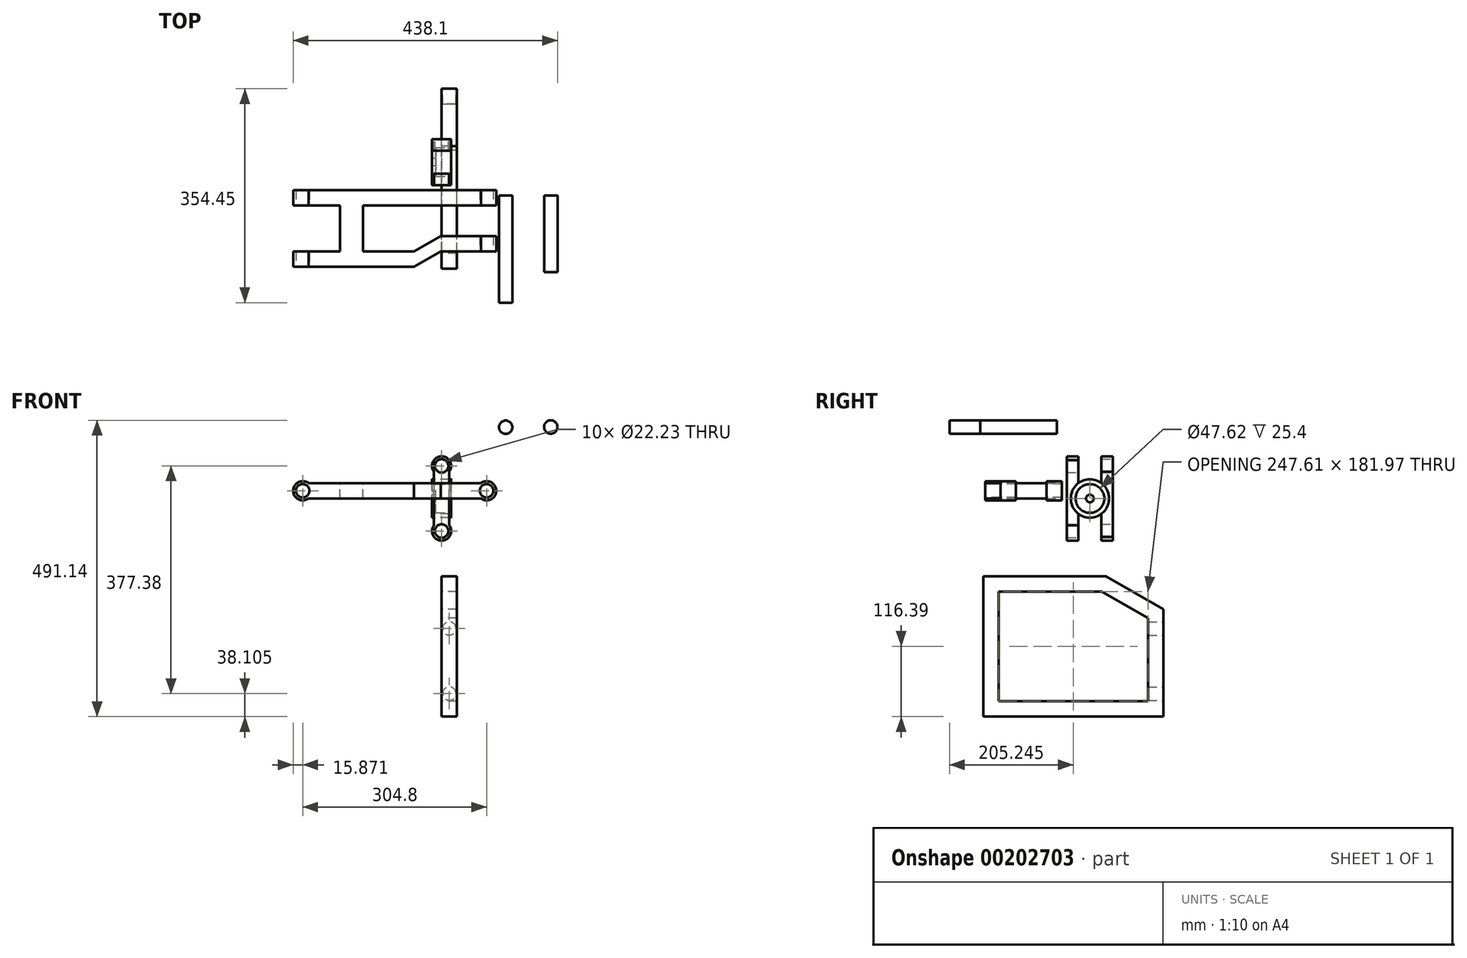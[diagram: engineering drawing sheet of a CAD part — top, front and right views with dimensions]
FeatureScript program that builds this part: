
annotation { "Feature Type Name" : "Feature", "Feature Type Description" : "" }
export const myFeature = defineFeature(function(context is Context, id is Id, definition is map)
    precondition{}
    {
        {
            var Q0;
            Q0=qCreatedBy(makeId("Top.planeOp"),FACE);
            var sketch = newSketch(context, id + "F0", { "sketchPlane" : qUnion([Q0])});
            skLineSegment(sketch, "E0.bottom", {"start": v(-230.2, 8.47) * mm, "end": v(74.6, 8.47) * mm});
            skLineSegment(sketch, "E0.top", {"start": v(-230.2, -16.93) * mm, "end": v(74.6, -16.93) * mm});
            skLineSegment(sketch, "E0.left", {"start": v(-230.2, 8.47) * mm, "end": v(-230.2, -16.93) * mm});
            skLineSegment(sketch, "E0.right", {"start": v(74.6, 8.47) * mm, "end": v(74.6, -16.93) * mm});
            skLineSegment(sketch, "E1", {"start": v(-77.8, -16.93) * mm, "end": v(-77.8, -93.13) * mm, "construction": true});
            skLineSegment(sketch, "E2", {"start": v(-230.2, -55.03) * mm, "end": v(91.79, -55.03) * mm, "construction": true});
            skPoint(sketch, "E2.startSnap0", {"position": v(-77.8, -55.03) * mm});
            skLineSegment(sketch, "E3.MirrorCS", {"start": v(-230.2, -118.53) * mm, "end": v(-45.6, -118.53) * mm});
            skLineSegment(sketch, "E4.MirrorCS", {"start": v(-230.2, -93.13) * mm, "end": v(-45.6, -93.13) * mm});
            skLineSegment(sketch, "E5.MirrorCS", {"start": v(-230.2, -118.53) * mm, "end": v(-230.2, -93.13) * mm});
            skLineSegment(sketch, "E6.bottom", {"start": v(74.6, -93.13) * mm, "end": v(74.6, -93.13) * mm});
            skLineSegment(sketch, "E6.top", {"start": v(74.6, -67.73) * mm, "end": v(74.6, -67.73) * mm});
            skLineSegment(sketch, "E6.left", {"start": v(74.6, -93.13) * mm, "end": v(74.6, -67.73) * mm});
            skLineSegment(sketch, "E6.right", {"start": v(74.6, -93.13) * mm, "end": v(74.6, -67.73) * mm});
            skLineSegment(sketch, "E7.bottom", {"start": v(74.6, -67.73) * mm, "end": v(-1.6, -67.73) * mm});
            skLineSegment(sketch, "E7.top", {"start": v(74.6, -67.73) * mm, "end": v(-1.6, -67.73) * mm});
            skLineSegment(sketch, "E7.right", {"start": v(-1.6, -67.73) * mm, "end": v(-1.6, -67.73) * mm});
            skLineSegment(sketch, "E8", {"start": v(-1.6, -67.73) * mm, "end": v(-45.6, -93.13) * mm});
            skLineSegment(sketch, "E9", {"start": v(-45.6, -118.53) * mm, "end": v(-1.6, -93.13) * mm});
            skLineSegment(sketch, "E10.trimOffspring", {"start": v(-1.6, -93.13) * mm, "end": v(74.6, -93.13) * mm});
            skSolve(sketch);
        }
        {
            var Q0;
            Q0 = qSketchRegion(id + "F0", true);
            extrude(context, id + "F1", {"entities" : qUnion([Q0]), "depth" : 25.4 * mm});
        }
        {
            var Q0;
            Q0=makeQuery(id+"F1.opExtrude","SWEPT_FACE",FACE,{"disambiguationData":[OSD([sQuery(id+"F0.wireOp",EDGE,"E3.MirrorCS")])]});
            var sketch = newSketch(context, id + "F2", { "sketchPlane" : qUnion([Q0])});
            skCircle(sketch, "E11", {"center": v(-230.2, 12.7) * mm, "radius": 15.88 * mm});
            skSolve(sketch);
        }
        {
            var Q0;
            Q0=makeQuery(id+"F1.opExtrude","SWEPT_FACE",FACE,{"disambiguationData":[OSD([sQuery(id+"F0.wireOp",EDGE,"E10.trimOffspring")])]});
            var sketch = newSketch(context, id + "F3", { "sketchPlane" : qUnion([Q0])});
            skCircle(sketch, "E12", {"center": v(74.6, 12.7) * mm, "radius": 15.88 * mm});
            skSolve(sketch);
        }
        {
            var Q0;
            {var subQ1=sQuery(id+"F0.wireOp",EDGE,"E3.MirrorCS");var subQ6=makeQuery(id+"F1.opExtrude","SWEPT_EDGE",EDGE,{"disambiguationData":[OSD([subQ1,sQuery(id+"F0.wireOp",EDGE,"E5.MirrorCS")])]});Q0=makeQuery(id+"F2.imprint","IMPRINT",FACE,{"disambiguationData":[TD([[makeQuery(id+"F2.imprint","IMPRINT",EDGE,{"derivedFrom":subQ6}),-1.0]])]});}
            extrude(context, id + "F4", {"entities" : qUnion([Q0]), "operationType" : NewBodyOperationType.ADD, "oppositeDirection" : true, "depth" : 25.4 * mm});
        }
        {
            var Q0;
            {var subQ1=sQuery(id+"F0.wireOp",EDGE,"E10.trimOffspring");var subQ6=makeQuery(id+"F1.opExtrude","SWEPT_EDGE",EDGE,{"disambiguationData":[OSD([sQuery(id+"F0.wireOp",EDGE,"E6.right"),subQ1])]});Q0=makeQuery(id+"F3.imprint","IMPRINT",FACE,{"disambiguationData":[TD([[makeQuery(id+"F3.imprint","IMPRINT",EDGE,{"derivedFrom":subQ6}),1.0]])]});}
            extrude(context, id + "F5", {"entities" : qUnion([Q0]), "operationType" : NewBodyOperationType.ADD, "oppositeDirection" : true, "depth" : 25.4 * mm});
        }
        {
            var Q0;
            Q0=makeQuery(id+"F1.opExtrude","SWEPT_FACE",FACE,{"disambiguationData":[OSD([sQuery(id+"F0.wireOp",EDGE,"E0.bottom")])]});
            var sketch = newSketch(context, id + "F6", { "sketchPlane" : qUnion([Q0])});
            skCircle(sketch, "E13", {"center": v(-74.6, 12.7) * mm, "radius": 15.88 * mm});
            skCircle(sketch, "E14", {"center": v(230.2, 12.7) * mm, "radius": 15.88 * mm});
            skSolve(sketch);
        }
        {
            var Q0;
            {var subQ1=sQuery(id+"F0.wireOp",EDGE,"E0.bottom");var subQ6=makeQuery(id+"F1.opExtrude","SWEPT_EDGE",EDGE,{"disambiguationData":[OSD([subQ1,sQuery(id+"F0.wireOp",EDGE,"E0.right")])]});Q0=makeQuery(id+"F6.imprint","IMPRINT",FACE,{"disambiguationData":[TD([[makeQuery(id+"F6.imprint","IMPRINT",EDGE,{"derivedFrom":subQ6}),-1.0]])]});}
            var Q1;
            {var subQ1=sQuery(id+"F0.wireOp",EDGE,"E0.bottom");var subQ6=makeQuery(id+"F1.opExtrude","SWEPT_EDGE",EDGE,{"disambiguationData":[OSD([subQ1,sQuery(id+"F0.wireOp",EDGE,"E0.left")])]});Q1=makeQuery(id+"F6.imprint","IMPRINT",FACE,{"disambiguationData":[TD([[makeQuery(id+"F6.imprint","IMPRINT",EDGE,{"derivedFrom":subQ6}),1.0]])]});}
            extrude(context, id + "F7", {"entities" : qUnion([Q0, Q1]), "operationType" : NewBodyOperationType.ADD, "oppositeDirection" : true, "depth" : 25.4 * mm});
        }
        {
            var Q0;
            {var subQ0=sQuery(id+"F0.wireOp",EDGE,"E3.MirrorCS");Q0=makeQuery(id+"F4.boolean.opBoolean","MERGE",FACE,{"derivedFrom":[makeQuery(id+"F1.opExtrude","SWEPT_FACE",FACE,{"disambiguationData":[OSD([subQ0])]}),makeQuery(id+"F4.opExtrude","CAP_FACE",FACE,{"disambiguationData":[OSD([subQ0,sQuery(id+"F0.wireOp",EDGE,"E5.MirrorCS"),sQuery(id+"F2.wireOp",EDGE,"E11")])],"isStart":true})]});}
            var sketch = newSketch(context, id + "F8", { "sketchPlane" : qUnion([Q0])});
            skCircle(sketch, "E15", {"center": v(-230.2, 12.7) * mm, "radius": 11.11 * mm});
            skSolve(sketch);
        }
        {
            var Q0;
            Q0=makeQuery(id+"F8.imprint","IMPRINT",FACE,{"disambiguationData":[TD([[makeQuery(id+"F8.imprint","IMPRINT",EDGE,{"derivedFrom":sQuery(id+"F8.wireOp",EDGE,"E15")}),1.0]])]});
            extrude(context, id + "F9", {"entities" : qUnion([Q0]), "operationType" : NewBodyOperationType.REMOVE, "endBound" : BoundingType.THROUGH_ALL, "oppositeDirection" : true, "depth" : 25.4 * mm});
        }
        {
            var Q0;
            {var subQ0=sQuery(id+"F0.wireOp",EDGE,"E10.trimOffspring");Q0=makeQuery(id+"F5.boolean.opBoolean","MERGE",FACE,{"derivedFrom":[makeQuery(id+"F1.opExtrude","SWEPT_FACE",FACE,{"disambiguationData":[OSD([subQ0])]}),makeQuery(id+"F5.opExtrude","CAP_FACE",FACE,{"disambiguationData":[OSD([sQuery(id+"F0.wireOp",EDGE,"E6.right"),subQ0,sQuery(id+"F3.wireOp",EDGE,"E12")])],"isStart":true})]});}
            var sketch = newSketch(context, id + "F10", { "sketchPlane" : qUnion([Q0])});
            skCircle(sketch, "E16", {"center": v(74.6, 12.7) * mm, "radius": 11.11 * mm});
            skSolve(sketch);
        }
        {
            var Q0;
            Q0=makeQuery(id+"F10.imprint","IMPRINT",FACE,{"disambiguationData":[TD([[makeQuery(id+"F10.imprint","IMPRINT",EDGE,{"derivedFrom":sQuery(id+"F10.wireOp",EDGE,"E16")}),1.0]])]});
            extrude(context, id + "F11", {"entities" : qUnion([Q0]), "operationType" : NewBodyOperationType.REMOVE, "endBound" : BoundingType.THROUGH_ALL, "oppositeDirection" : true, "depth" : 25.4 * mm});
        }
        {
            var Q0;
            {var subQ0=sQuery(id+"F0.wireOp",EDGE,"E0.bottom");Q0=makeQuery(id+"F7.boolean.opBoolean","MERGE",FACE,{"derivedFrom":[makeQuery(id+"F1.opExtrude","SWEPT_FACE",FACE,{"disambiguationData":[OSD([subQ0])]}),makeQuery(id+"F7.opExtrude","CAP_FACE",FACE,{"disambiguationData":[OSD([subQ0,sQuery(id+"F0.wireOp",EDGE,"E0.right"),sQuery(id+"F6.wireOp",EDGE,"E13")])],"isStart":true}),makeQuery(id+"F7.opExtrude","CAP_FACE",FACE,{"disambiguationData":[OSD([subQ0,sQuery(id+"F0.wireOp",EDGE,"E0.left"),sQuery(id+"F6.wireOp",EDGE,"E14")])],"isStart":true})]});}
            var sketch = newSketch(context, id + "F12", { "sketchPlane" : qUnion([Q0])});
            skCircle(sketch, "E17", {"center": v(-74.6, 12.7) * mm, "radius": 11.11 * mm});
            skCircle(sketch, "E18", {"center": v(230.2, 12.7) * mm, "radius": 11.11 * mm});
            skSolve(sketch);
        }
        {
            var Q0;
            Q0=makeQuery(id+"F12.imprint","IMPRINT",FACE,{"disambiguationData":[TD([[makeQuery(id+"F12.imprint","IMPRINT",EDGE,{"derivedFrom":sQuery(id+"F12.wireOp",EDGE,"E17")}),1.0]])]});
            var Q1;
            Q1=makeQuery(id+"F12.imprint","IMPRINT",FACE,{"disambiguationData":[TD([[makeQuery(id+"F12.imprint","IMPRINT",EDGE,{"derivedFrom":sQuery(id+"F12.wireOp",EDGE,"E18")}),1.0]])]});
            extrude(context, id + "F13", {"entities" : qUnion([Q0, Q1]), "operationType" : NewBodyOperationType.REMOVE, "endBound" : BoundingType.THROUGH_ALL, "oppositeDirection" : true, "depth" : 25.4 * mm});
        }
        {
            var Q0;
            Q0=makeQuery(id+"F1.opExtrude","CAP_FACE",FACE,{"disambiguationData":[OSD([sQuery(id+"F0.wireOp",EDGE,"E0.bottom"),sQuery(id+"F0.wireOp",EDGE,"E0.top"),sQuery(id+"F0.wireOp",EDGE,"E0.left"),sQuery(id+"F0.wireOp",EDGE,"E0.right")])],"isStart":false});
            var sketch = newSketch(context, id + "F14", { "sketchPlane" : qUnion([Q0])});
            skLineSegment(sketch, "E19", {"start": v(-77.8, -16.93) * mm, "end": v(-220.68, -16.93) * mm});
            skLineSegment(sketch, "E20.bottom", {"start": v(-168.3, -10.98) * mm, "end": v(-130.2, -10.98) * mm});
            skLineSegment(sketch, "E20.top", {"start": v(-168.3, -103.03) * mm, "end": v(-130.2, -103.03) * mm});
            skLineSegment(sketch, "E20.left", {"start": v(-168.3, -10.98) * mm, "end": v(-168.3, -103.03) * mm});
            skLineSegment(sketch, "E20.right", {"start": v(-130.2, -10.98) * mm, "end": v(-130.2, -103.03) * mm});
            skLineSegment(sketch, "E21", {"start": v(-149.25, -16.93) * mm, "end": v(-149.25, -93.19) * mm, "construction": true});
            skSolve(sketch);
        }
        {
            var Q0;
            {var subQ5=sQuery(id+"F14.wireOp",EDGE,"E20.top");Q0=makeQuery(id+"F14.imprint","IMPRINT",FACE,{"disambiguationData":[TD([[makeQuery(id+"F14.imprint","IMPRINT",EDGE,{"derivedFrom":subQ5}),1.0]])]});}
            extrude(context, id + "F15", {"entities" : qUnion([Q0]), "operationType" : NewBodyOperationType.ADD, "oppositeDirection" : true, "depth" : 25.4 * mm});
        }
        {
            var Q0;
            Q0=makeQuery(id+"F15.opExtrude","SWEPT_FACE",FACE,{"disambiguationData":[OSD([sQuery(id+"F14.wireOp",EDGE,"E20.left")])]});
            extrude(context, id + "F16", {"entities" : qUnion([Q0]), "depth" : 25.4 * mm});
        }
        {
            var Q0;
            Q0=makeQuery(id+"F16.opExtrude","SWEPT_BODY",BODY,{"disambiguationData":[OSD([sQuery(id+"F14.wireOp",EDGE,"E20.left")])]});
            deleteBodies(context, id + "F17", {"entities" : qUnion([Q0])});
        }
        {
            var Q0;
            Q0=qCreatedBy(makeId("Right.planeOp"),FACE);
            var sketch = newSketch(context, id + "F18", { "sketchPlane" : qUnion([Q0])});
            skLineSegment(sketch, "E22", {"start": v(17, 63.5) * mm, "end": v(36.05, 63.5) * mm});
            skLineSegment(sketch, "E23", {"start": v(36.05, 63.5) * mm, "end": v(36.05, 12.7) * mm});
            skLineSegment(sketch, "E24", {"start": v(36.05, 12.7) * mm, "end": v(74.15, 12.7) * mm});
            skLineSegment(sketch, "E25", {"start": v(74.15, 12.7) * mm, "end": v(74.15, 63.5) * mm});
            skLineSegment(sketch, "E26", {"start": v(74.15, 63.5) * mm, "end": v(93.2, 63.5) * mm});
            skLineSegment(sketch, "E27", {"start": v(93.2, 63.5) * mm, "end": v(93.2, -63.5) * mm});
            skLineSegment(sketch, "E28", {"start": v(93.2, -63.5) * mm, "end": v(74.15, -63.5) * mm});
            skLineSegment(sketch, "E29", {"start": v(74.15, -63.5) * mm, "end": v(74.15, -12.7) * mm});
            skLineSegment(sketch, "E30", {"start": v(74.15, -12.7) * mm, "end": v(36.05, -12.7) * mm});
            skLineSegment(sketch, "E31", {"start": v(36.05, -12.7) * mm, "end": v(36.05, -63.5) * mm});
            skLineSegment(sketch, "E32", {"start": v(36.05, -63.5) * mm, "end": v(17, -63.5) * mm});
            skLineSegment(sketch, "E33", {"start": v(17, -63.5) * mm, "end": v(17, 63.5) * mm});
            skCircle(sketch, "E34", {"center": v(55.1, 0) * mm, "radius": 31.75 * mm});
            skPoint(sketch, "E34.centerSnap0", {"position": v(55.1, 12.7) * mm});
            skCircle(sketch, "E35", {"center": v(55.1, 0) * mm, "radius": 6.35 * mm});
            skSolve(sketch);
        }
        {
            var Q0;
            {var subQ2=sQuery(id+"F18.wireOp",EDGE,"E22");Q0=makeQuery(id+"F18.imprint","IMPRINT",FACE,{"disambiguationData":[TD([[makeQuery(id+"F18.imprint","IMPRINT",EDGE,{"derivedFrom":subQ2}),-1.0]])]});}
            extrude(context, id + "F19", {"entities" : qUnion([Q0]), "endBound" : BoundingType.SYMMETRIC, "depth" : 25.4 * mm});
        }
        {
            var Q0;
            {var subQ4=sQuery(id+"F18.wireOp",EDGE,"E26");Q0=makeQuery(id+"F18.imprint","IMPRINT",FACE,{"disambiguationData":[TD([[makeQuery(id+"F18.imprint","IMPRINT",EDGE,{"derivedFrom":subQ4}),-1.0]])]});}
            extrude(context, id + "F20", {"entities" : qUnion([Q0]), "operationType" : NewBodyOperationType.ADD, "endBound" : BoundingType.SYMMETRIC, "depth" : 25.4 * mm});
        }
        {
            var Q0;
            {var subQ0=sQuery(id+"F18.wireOp",EDGE,"E24");Q0=makeQuery(id+"F18.imprint","IMPRINT",FACE,{"disambiguationData":[TD([[makeQuery(id+"F18.imprint","IMPRINT",EDGE,{"derivedFrom":subQ0}),1.0]])]});}
            var Q1;
            {var subQ1=sQuery(id+"F18.wireOp",EDGE,"E24");Q1=makeQuery(id+"F18.imprint","IMPRINT",FACE,{"disambiguationData":[TD([[makeQuery(id+"F18.imprint","IMPRINT",EDGE,{"derivedFrom":subQ1}),-1.0]])]});}
            var Q2;
            {var subQ0=sQuery(id+"F18.wireOp",EDGE,"E30");Q2=makeQuery(id+"F18.imprint","IMPRINT",FACE,{"disambiguationData":[TD([[makeQuery(id+"F18.imprint","IMPRINT",EDGE,{"derivedFrom":subQ0}),1.0]])]});}
            var Q3;
            {var subQ2=sQuery(id+"F18.wireOp",EDGE,"E23");var subQ4=sQuery(id+"F18.wireOp",EDGE,"E34");var subQ5=makeQuery(id+"F18.imprint","INTERSECT",VERTEX,{"derivedFrom":[subQ2,subQ4]});Q3=makeQuery(id+"F18.imprint","IMPRINT",FACE,{"disambiguationData":[TD([[makeQuery(id+"F18.imprint","IMPRINT",EDGE,{"disambiguationData":[TD([[subQ5,1.0]])],"derivedFrom":subQ4}),1.0]])]});}
            var Q4;
            {var subQ1=sQuery(id+"F18.wireOp",EDGE,"E23");var subQ3=sQuery(id+"F18.wireOp",EDGE,"E34");var subQ4=makeQuery(id+"F18.imprint","INTERSECT",VERTEX,{"derivedFrom":[subQ1,subQ3]});Q4=makeQuery(id+"F18.imprint","IMPRINT",FACE,{"disambiguationData":[TD([[makeQuery(id+"F18.imprint","IMPRINT",EDGE,{"disambiguationData":[TD([[subQ4,-1.0]])],"derivedFrom":subQ3}),1.0]])]});}
            var Q5;
            {var subQ2=sQuery(id+"F18.wireOp",EDGE,"E29");var subQ4=sQuery(id+"F18.wireOp",EDGE,"E34");var subQ5=makeQuery(id+"F18.imprint","INTERSECT",VERTEX,{"derivedFrom":[subQ2,subQ4]});Q5=makeQuery(id+"F18.imprint","IMPRINT",FACE,{"disambiguationData":[TD([[makeQuery(id+"F18.imprint","IMPRINT",EDGE,{"disambiguationData":[TD([[subQ5,1.0]])],"derivedFrom":subQ4}),1.0]])]});}
            var Q6;
            {var subQ1=sQuery(id+"F18.wireOp",EDGE,"E25");var subQ3=sQuery(id+"F18.wireOp",EDGE,"E34");var subQ4=makeQuery(id+"F18.imprint","INTERSECT",VERTEX,{"derivedFrom":[subQ1,subQ3]});Q6=makeQuery(id+"F18.imprint","IMPRINT",FACE,{"disambiguationData":[TD([[makeQuery(id+"F18.imprint","IMPRINT",EDGE,{"disambiguationData":[TD([[subQ4,1.0]])],"derivedFrom":subQ3}),1.0]])]});}
            extrude(context, id + "F21", {"entities" : qUnion([Q0, Q1, Q2, Q3, Q4, Q5, Q6]), "operationType" : NewBodyOperationType.ADD, "endBound" : BoundingType.SYMMETRIC, "depth" : 31.75 * mm});
        }
        {
            var Q0;
            Q0=makeQuery(id+"F20.opExtrude","SWEPT_FACE",FACE,{"disambiguationData":[OSD([sQuery(id+"F18.wireOp",EDGE,"E27")])]});
            var sketch = newSketch(context, id + "F22", { "sketchPlane" : qUnion([Q0])});
            skCircle(sketch, "E36", {"center": v(0, 53.97) * mm, "radius": 15.88 * mm});
            skPoint(sketch, "E37", {"position": v(0, 63.5) * mm});
            skLineSegment(sketch, "E38", {"start": v(12.7, 0) * mm, "end": v(-12.7, 0) * mm, "construction": true});
            skCircle(sketch, "E39.MirrorC", {"center": v(0, -53.98) * mm, "radius": 15.88 * mm});
            skCircle(sketch, "E40", {"center": v(0, 53.97) * mm, "radius": 11.11 * mm});
            skCircle(sketch, "E41", {"center": v(0, -53.98) * mm, "radius": 11.11 * mm});
            skSolve(sketch);
        }
        {
            var Q0;
            {var subQ0=sQuery(id+"F22.wireOp",EDGE,"E36");var subQ1=sQuery(id+"F18.wireOp",EDGE,"E27");var subQ8=makeQuery(id+"F20.opExtrude","CAP_EDGE",EDGE,{"disambiguationData":[OSD([subQ1])],"isStart":false});var subQ10=makeQuery(id+"F22.imprint","INTERSECT",VERTEX,{"derivedFrom":[subQ8,subQ0]});Q0=makeQuery(id+"F22.imprint","IMPRINT",FACE,{"disambiguationData":[TD([[makeQuery(id+"F22.imprint","IMPRINT",EDGE,{"disambiguationData":[TD([[subQ10,-1.0]])],"derivedFrom":subQ0}),1.0]])]});}
            var Q1;
            {var subQ0=sQuery(id+"F22.wireOp",EDGE,"E36");var subQ1=sQuery(id+"F18.wireOp",EDGE,"E27");var subQ2=makeQuery(id+"F20.opExtrude","CAP_EDGE",EDGE,{"disambiguationData":[OSD([subQ1])],"isStart":false});var subQ4=makeQuery(id+"F22.imprint","INTERSECT",VERTEX,{"derivedFrom":[subQ2,subQ0]});Q1=makeQuery(id+"F22.imprint","IMPRINT",FACE,{"disambiguationData":[TD([[makeQuery(id+"F22.imprint","IMPRINT",EDGE,{"disambiguationData":[TD([[subQ4,1.0]])],"derivedFrom":subQ0}),1.0]])]});}
            var Q2;
            {var subQ0=sQuery(id+"F22.wireOp",EDGE,"E36");var subQ1=sQuery(id+"F18.wireOp",EDGE,"E27");var subQ2=makeQuery(id+"F20.opExtrude","CAP_EDGE",EDGE,{"disambiguationData":[OSD([subQ1])],"isStart":true});var subQ4=makeQuery(id+"F22.imprint","INTERSECT",VERTEX,{"derivedFrom":[subQ2,subQ0]});Q2=makeQuery(id+"F22.imprint","IMPRINT",FACE,{"disambiguationData":[TD([[makeQuery(id+"F22.imprint","IMPRINT",EDGE,{"disambiguationData":[TD([[subQ4,-1.0]])],"derivedFrom":subQ0}),1.0]])]});}
            var Q3;
            {var subQ1=sQuery(id+"F18.wireOp",EDGE,"E27");var subQ2=makeQuery(id+"F20.opExtrude","SWEPT_EDGE",EDGE,{"disambiguationData":[OSD([sQuery(id+"F18.wireOp",EDGE,"E26"),subQ1])]});var subQ5=sQuery(id+"F22.wireOp",EDGE,"E40");var subQ6=makeQuery(id+"F22.imprint","INTERSECT",VERTEX,{"disambiguationData":[OD(0.0)],"derivedFrom":[subQ2,subQ5]});Q3=makeQuery(id+"F22.imprint","IMPRINT",FACE,{"disambiguationData":[TD([[makeQuery(id+"F22.imprint","IMPRINT",EDGE,{"disambiguationData":[TD([[subQ6,-1.0]])],"derivedFrom":subQ5}),-1.0]])]});}
            var Q4;
            {var subQ0=sQuery(id+"F22.wireOp",EDGE,"E40");var subQ1=makeQuery(id+"F20.opExtrude","SWEPT_EDGE",EDGE,{"disambiguationData":[OSD([sQuery(id+"F18.wireOp",EDGE,"E26"),sQuery(id+"F18.wireOp",EDGE,"E27")])]});var subQ2=makeQuery(id+"F22.imprint","INTERSECT",VERTEX,{"disambiguationData":[OD(0.0)],"derivedFrom":[subQ1,subQ0]});Q4=makeQuery(id+"F22.imprint","IMPRINT",FACE,{"disambiguationData":[TD([[makeQuery(id+"F22.imprint","IMPRINT",EDGE,{"disambiguationData":[TD([[subQ2,-1.0]])],"derivedFrom":subQ0}),1.0]])]});}
            var Q5;
            {var subQ0=sQuery(id+"F22.wireOp",EDGE,"E39.MirrorC");var subQ1=sQuery(id+"F18.wireOp",EDGE,"E27");var subQ2=makeQuery(id+"F20.opExtrude","CAP_EDGE",EDGE,{"disambiguationData":[OSD([subQ1])],"isStart":true});var subQ4=makeQuery(id+"F22.imprint","INTERSECT",VERTEX,{"derivedFrom":[subQ2,subQ0]});Q5=makeQuery(id+"F22.imprint","IMPRINT",FACE,{"disambiguationData":[TD([[makeQuery(id+"F22.imprint","IMPRINT",EDGE,{"disambiguationData":[TD([[subQ4,-1.0]])],"derivedFrom":subQ0}),-1.0]])]});}
            var Q6;
            {var subQ0=sQuery(id+"F22.wireOp",EDGE,"E39.MirrorC");var subQ1=sQuery(id+"F18.wireOp",EDGE,"E27");var subQ2=makeQuery(id+"F20.opExtrude","CAP_EDGE",EDGE,{"disambiguationData":[OSD([subQ1])],"isStart":false});var subQ10=makeQuery(id+"F22.imprint","INTERSECT",VERTEX,{"derivedFrom":[subQ2,subQ0]});Q6=makeQuery(id+"F22.imprint","IMPRINT",FACE,{"disambiguationData":[TD([[makeQuery(id+"F22.imprint","IMPRINT",EDGE,{"disambiguationData":[TD([[subQ10,-1.0]])],"derivedFrom":subQ0}),-1.0]])]});}
            var Q7;
            {var subQ1=sQuery(id+"F18.wireOp",EDGE,"E27");var subQ2=makeQuery(id+"F20.opExtrude","SWEPT_EDGE",EDGE,{"disambiguationData":[OSD([subQ1,sQuery(id+"F18.wireOp",EDGE,"E28")])]});var subQ5=sQuery(id+"F22.wireOp",EDGE,"E41");var subQ6=makeQuery(id+"F22.imprint","INTERSECT",VERTEX,{"disambiguationData":[OD(0.0)],"derivedFrom":[subQ2,subQ5]});Q7=makeQuery(id+"F22.imprint","IMPRINT",FACE,{"disambiguationData":[TD([[makeQuery(id+"F22.imprint","IMPRINT",EDGE,{"disambiguationData":[TD([[subQ6,1.0]])],"derivedFrom":subQ5}),-1.0]])]});}
            var Q8;
            {var subQ0=sQuery(id+"F22.wireOp",EDGE,"E39.MirrorC");var subQ1=sQuery(id+"F18.wireOp",EDGE,"E27");var subQ2=makeQuery(id+"F20.opExtrude","CAP_EDGE",EDGE,{"disambiguationData":[OSD([subQ1])],"isStart":false});var subQ4=makeQuery(id+"F22.imprint","INTERSECT",VERTEX,{"derivedFrom":[subQ2,subQ0]});Q8=makeQuery(id+"F22.imprint","IMPRINT",FACE,{"disambiguationData":[TD([[makeQuery(id+"F22.imprint","IMPRINT",EDGE,{"disambiguationData":[TD([[subQ4,1.0]])],"derivedFrom":subQ0}),-1.0]])]});}
            extrude(context, id + "F23", {"entities" : qUnion([Q0, Q1, Q2, Q3, Q4, Q5, Q6, Q7, Q8]), "operationType" : NewBodyOperationType.ADD, "oppositeDirection" : true, "depth" : 19.05 * mm});
        }
        {
            var Q0;
            {var subQ0=sQuery(id+"F22.wireOp",EDGE,"E40");var subQ1=makeQuery(id+"F20.opExtrude","SWEPT_EDGE",EDGE,{"disambiguationData":[OSD([sQuery(id+"F18.wireOp",EDGE,"E26"),sQuery(id+"F18.wireOp",EDGE,"E27")])]});var subQ2=makeQuery(id+"F22.imprint","INTERSECT",VERTEX,{"disambiguationData":[OD(0.0)],"derivedFrom":[subQ1,subQ0]});Q0=makeQuery(id+"F22.imprint","IMPRINT",FACE,{"disambiguationData":[TD([[makeQuery(id+"F22.imprint","IMPRINT",EDGE,{"disambiguationData":[TD([[subQ2,1.0]])],"derivedFrom":subQ0}),1.0]])]});}
            var Q1;
            {var subQ0=sQuery(id+"F22.wireOp",EDGE,"E40");var subQ1=makeQuery(id+"F20.opExtrude","SWEPT_EDGE",EDGE,{"disambiguationData":[OSD([sQuery(id+"F18.wireOp",EDGE,"E26"),sQuery(id+"F18.wireOp",EDGE,"E27")])]});var subQ2=makeQuery(id+"F22.imprint","INTERSECT",VERTEX,{"disambiguationData":[OD(0.0)],"derivedFrom":[subQ1,subQ0]});Q1=makeQuery(id+"F22.imprint","IMPRINT",FACE,{"disambiguationData":[TD([[makeQuery(id+"F22.imprint","IMPRINT",EDGE,{"disambiguationData":[TD([[subQ2,-1.0]])],"derivedFrom":subQ0}),1.0]])]});}
            var Q2;
            {var subQ0=sQuery(id+"F22.wireOp",EDGE,"E41");var subQ1=makeQuery(id+"F20.opExtrude","SWEPT_EDGE",EDGE,{"disambiguationData":[OSD([sQuery(id+"F18.wireOp",EDGE,"E27"),sQuery(id+"F18.wireOp",EDGE,"E28")])]});var subQ2=makeQuery(id+"F22.imprint","INTERSECT",VERTEX,{"disambiguationData":[OD(0.0)],"derivedFrom":[subQ1,subQ0]});Q2=makeQuery(id+"F22.imprint","IMPRINT",FACE,{"disambiguationData":[TD([[makeQuery(id+"F22.imprint","IMPRINT",EDGE,{"disambiguationData":[TD([[subQ2,-1.0]])],"derivedFrom":subQ0}),1.0]])]});}
            var Q3;
            {var subQ0=sQuery(id+"F22.wireOp",EDGE,"E41");var subQ1=makeQuery(id+"F20.opExtrude","SWEPT_EDGE",EDGE,{"disambiguationData":[OSD([sQuery(id+"F18.wireOp",EDGE,"E27"),sQuery(id+"F18.wireOp",EDGE,"E28")])]});var subQ2=makeQuery(id+"F22.imprint","INTERSECT",VERTEX,{"disambiguationData":[OD(0.0)],"derivedFrom":[subQ1,subQ0]});Q3=makeQuery(id+"F22.imprint","IMPRINT",FACE,{"disambiguationData":[TD([[makeQuery(id+"F22.imprint","IMPRINT",EDGE,{"disambiguationData":[TD([[subQ2,1.0]])],"derivedFrom":subQ0}),1.0]])]});}
            extrude(context, id + "F24", {"entities" : qUnion([Q0, Q1, Q2, Q3]), "operationType" : NewBodyOperationType.REMOVE, "endBound" : BoundingType.THROUGH_ALL, "oppositeDirection" : true, "depth" : 25.4 * mm});
        }
        {
            var Q0;
            Q0=makeQuery(id+"F19.opExtrude","SWEPT_FACE",FACE,{"disambiguationData":[OSD([sQuery(id+"F18.wireOp",EDGE,"E33")])]});
            var sketch = newSketch(context, id + "F25", { "sketchPlane" : qUnion([Q0])});
            skCircle(sketch, "E42.MirrorC", {"center": v(0, 53.98) * mm, "radius": 15.88 * mm});
            skCircle(sketch, "E43", {"center": v(0, 53.98) * mm, "radius": 11.11 * mm});
            skLineSegment(sketch, "E44", {"start": v(0, 53.98) * mm, "end": v(0, 53.98) * mm});
            skCircle(sketch, "E45", {"center": v(0, -53.97) * mm, "radius": 15.88 * mm});
            skCircle(sketch, "E46", {"center": v(0, -53.97) * mm, "radius": 11.11 * mm});
            skSolve(sketch);
        }
        {
            var Q0;
            {var subQ1=sQuery(id+"F18.wireOp",EDGE,"E22");var subQ3=sQuery(id+"F18.wireOp",EDGE,"E33");var subQ5=sQuery(id+"F18.wireOp",EDGE,"E34");var subQ6=sQuery(id+"F18.wireOp",EDGE,"E32");var subQ7=sQuery(id+"F18.wireOp",EDGE,"E31");var subQ8=sQuery(id+"F18.wireOp",EDGE,"E23");var subQ10=makeQuery(id+"F19.opExtrude","SWEPT_EDGE",EDGE,{"disambiguationData":[OSD([subQ1,subQ3])]});var subQ11=makeQuery(id+"F24.boolean.opBoolean","SPLIT",EDGE,{"disambiguationData":[TD([makeQuery(id+"F19.opExtrude","CAP_FACE",FACE,{"disambiguationData":[OSD([subQ1,subQ8,subQ7,subQ6,subQ3,subQ5])],"isStart":true})])],"derivedFrom":subQ10});Q0=makeQuery(id+"F25.imprint","IMPRINT",FACE,{"disambiguationData":[TD([[makeQuery(id+"F25.imprint","IMPRINT",EDGE,{"derivedFrom":subQ11}),-1.0]])]});}
            var Q1;
            {var subQ0=sQuery(id+"F25.wireOp",EDGE,"E42.MirrorC");var subQ2=sQuery(id+"F18.wireOp",EDGE,"E33");var subQ3=makeQuery(id+"F19.opExtrude","CAP_EDGE",EDGE,{"disambiguationData":[OSD([subQ2])],"isStart":true});var subQ5=makeQuery(id+"F25.imprint","INTERSECT",VERTEX,{"derivedFrom":[subQ3,subQ0]});Q1=makeQuery(id+"F25.imprint","IMPRINT",FACE,{"disambiguationData":[TD([[makeQuery(id+"F25.imprint","IMPRINT",EDGE,{"disambiguationData":[TD([[subQ5,-1.0]])],"derivedFrom":subQ0}),-1.0]])]});}
            var Q2;
            {var subQ0=sQuery(id+"F25.wireOp",EDGE,"E42.MirrorC");var subQ2=sQuery(id+"F18.wireOp",EDGE,"E33");var subQ3=makeQuery(id+"F19.opExtrude","CAP_EDGE",EDGE,{"disambiguationData":[OSD([subQ2])],"isStart":false});var subQ5=makeQuery(id+"F25.imprint","INTERSECT",VERTEX,{"derivedFrom":[subQ3,subQ0]});Q2=makeQuery(id+"F25.imprint","IMPRINT",FACE,{"disambiguationData":[TD([[makeQuery(id+"F25.imprint","IMPRINT",EDGE,{"disambiguationData":[TD([[subQ5,1.0]])],"derivedFrom":subQ0}),-1.0]])]});}
            var Q3;
            {var subQ0=sQuery(id+"F25.wireOp",EDGE,"E45");var subQ1=sQuery(id+"F18.wireOp",EDGE,"E33");var subQ3=makeQuery(id+"F19.opExtrude","CAP_EDGE",EDGE,{"disambiguationData":[OSD([subQ1])],"isStart":true});var subQ5=makeQuery(id+"F25.imprint","INTERSECT",VERTEX,{"derivedFrom":[subQ3,subQ0]});Q3=makeQuery(id+"F25.imprint","IMPRINT",FACE,{"disambiguationData":[TD([[makeQuery(id+"F25.imprint","IMPRINT",EDGE,{"disambiguationData":[TD([[subQ5,-1.0]])],"derivedFrom":subQ0}),1.0]])]});}
            var Q4;
            {var subQ0=sQuery(id+"F25.wireOp",EDGE,"E45");var subQ1=sQuery(id+"F18.wireOp",EDGE,"E33");var subQ3=makeQuery(id+"F19.opExtrude","CAP_EDGE",EDGE,{"disambiguationData":[OSD([subQ1])],"isStart":false});var subQ5=makeQuery(id+"F25.imprint","INTERSECT",VERTEX,{"derivedFrom":[subQ3,subQ0]});Q4=makeQuery(id+"F25.imprint","IMPRINT",FACE,{"disambiguationData":[TD([[makeQuery(id+"F25.imprint","IMPRINT",EDGE,{"disambiguationData":[TD([[subQ5,1.0]])],"derivedFrom":subQ0}),1.0]])]});}
            var Q5;
            {var subQ3=sQuery(id+"F18.wireOp",EDGE,"E33");var subQ12=sQuery(id+"F25.wireOp",EDGE,"E42.MirrorC");var subQ16=makeQuery(id+"F19.opExtrude","CAP_EDGE",EDGE,{"disambiguationData":[OSD([subQ3])],"isStart":true});var subQ17=makeQuery(id+"F25.imprint","INTERSECT",VERTEX,{"derivedFrom":[subQ16,subQ12]});Q5=makeQuery(id+"F25.imprint","IMPRINT",FACE,{"disambiguationData":[TD([[makeQuery(id+"F25.imprint","IMPRINT",EDGE,{"disambiguationData":[TD([[subQ17,1.0]])],"derivedFrom":subQ12}),-1.0]])]});}
            var Q6;
            {var subQ1=sQuery(id+"F18.wireOp",EDGE,"E33");var subQ13=sQuery(id+"F25.wireOp",EDGE,"E45");var subQ14=makeQuery(id+"F19.opExtrude","CAP_EDGE",EDGE,{"disambiguationData":[OSD([subQ1])],"isStart":true});var subQ15=makeQuery(id+"F25.imprint","INTERSECT",VERTEX,{"derivedFrom":[subQ14,subQ13]});Q6=makeQuery(id+"F25.imprint","IMPRINT",FACE,{"disambiguationData":[TD([[makeQuery(id+"F25.imprint","IMPRINT",EDGE,{"disambiguationData":[TD([[subQ15,1.0]])],"derivedFrom":subQ13}),1.0]])]});}
            var Q7;
            {var subQ1=sQuery(id+"F18.wireOp",EDGE,"E34");var subQ2=sQuery(id+"F18.wireOp",EDGE,"E33");var subQ3=sQuery(id+"F18.wireOp",EDGE,"E32");var subQ4=sQuery(id+"F18.wireOp",EDGE,"E31");var subQ5=sQuery(id+"F18.wireOp",EDGE,"E23");var subQ6=sQuery(id+"F18.wireOp",EDGE,"E22");var subQ10=makeQuery(id+"F19.opExtrude","SWEPT_EDGE",EDGE,{"disambiguationData":[OSD([subQ3,subQ2])]});var subQ11=makeQuery(id+"F24.boolean.opBoolean","SPLIT",EDGE,{"disambiguationData":[TD([makeQuery(id+"F19.opExtrude","CAP_FACE",FACE,{"disambiguationData":[OSD([subQ6,subQ5,subQ4,subQ3,subQ2,subQ1])],"isStart":true})])],"derivedFrom":subQ10});Q7=makeQuery(id+"F25.imprint","IMPRINT",FACE,{"disambiguationData":[TD([[makeQuery(id+"F25.imprint","IMPRINT",EDGE,{"derivedFrom":subQ11}),1.0]])]});}
            extrude(context, id + "F26", {"entities" : qUnion([Q0, Q1, Q2, Q3, Q4, Q5, Q6, Q7]), "operationType" : NewBodyOperationType.ADD, "oppositeDirection" : true, "depth" : 19.05 * mm});
        }
        {
            var Q0;
            Q0=makeQuery(id+"F21.opExtrude","CAP_FACE",FACE,{"disambiguationData":[OSD([sQuery(id+"F18.wireOp",EDGE,"E34"),sQuery(id+"F18.wireOp",EDGE,"E35")])],"isStart":false});
            var sketch = newSketch(context, id + "F27", { "sketchPlane" : qUnion([Q0])});
            skCircle(sketch, "E47", {"center": v(55.1, 0) * mm, "radius": 23.81 * mm});
            skSolve(sketch);
        }
        {
            var Q0;
            Q0 = qSketchRegion(id + "F27", true);
            extrude(context, id + "F28", {"entities" : qUnion([Q0]), "operationType" : NewBodyOperationType.REMOVE, "oppositeDirection" : true, "depth" : 25.4 * mm});
        }
        {
            var Q0;
            Q0=qCreatedBy(makeId("Front.planeOp"),FACE);
            var sketch = newSketch(context, id + "F29", { "sketchPlane" : qUnion([Q0])});
            skCircle(sketch, "E48", {"center": v(180.91, 118.51) * mm, "radius": 11.11 * mm});
            skSolve(sketch);
        }
        {
            var Q0;
            Q0=makeQuery(id+"F29.imprint","IMPRINT",FACE,{"disambiguationData":[TD([[makeQuery(id+"F29.imprint","IMPRINT",EDGE,{"derivedFrom":sQuery(id+"F29.wireOp",EDGE,"E48")}),1.0]])]});
            extrude(context, id + "F30", {"entities" : qUnion([Q0]), "depth" : 127 * mm});
        }
        {
            var Q0;
            Q0=qCreatedBy(makeId("Front.planeOp"),FACE);
            var sketch = newSketch(context, id + "F31", { "sketchPlane" : qUnion([Q0])});
            skCircle(sketch, "E49", {"center": v(106.15, 118.07) * mm, "radius": 11.11 * mm});
            skSolve(sketch);
        }
        {
            var Q0;
            Q0=qCreatedBy(makeId("Right.planeOp"),FACE);
            var sketch = newSketch(context, id + "F32", { "sketchPlane" : qUnion([Q0])});
            skLineSegment(sketch, "E50", {"start": v(-121.76, -128.74) * mm, "end": v(81.44, -128.74) * mm});
            skLineSegment(sketch, "E51", {"start": v(81.44, -128.74) * mm, "end": v(176.65, -183.7) * mm});
            skLineSegment(sketch, "E52", {"start": v(176.65, -183.7) * mm, "end": v(176.65, -361.5) * mm});
            skLineSegment(sketch, "E53", {"start": v(176.65, -361.5) * mm, "end": v(-121.76, -361.5) * mm});
            skLineSegment(sketch, "E54", {"start": v(-121.76, -361.5) * mm, "end": v(-121.76, -128.74) * mm});
            skLineSegment(sketch, "E55.0", {"start": v(-96.36, -154.14) * mm, "end": v(74.63, -154.14) * mm});
            skLineSegment(sketch, "E56.0", {"start": v(74.63, -154.14) * mm, "end": v(151.25, -198.37) * mm});
            skLineSegment(sketch, "E57.0", {"start": v(151.25, -198.37) * mm, "end": v(151.25, -336.1) * mm});
            skLineSegment(sketch, "E58.0", {"start": v(151.25, -336.1) * mm, "end": v(-96.36, -336.1) * mm});
            skLineSegment(sketch, "E59.0", {"start": v(-121.76, -310.7) * mm, "end": v(-121.76, -128.74) * mm});
            skLineSegment(sketch, "E60.0", {"start": v(-96.36, -336.1) * mm, "end": v(-96.36, -154.14) * mm});
            skSolve(sketch);
        }
        {
            var Q0;
            {var subQ3=sQuery(id+"F32.wireOp",EDGE,"E50");Q0=makeQuery(id+"F32.imprint","IMPRINT",FACE,{"disambiguationData":[TD([[makeQuery(id+"F32.imprint","IMPRINT",EDGE,{"derivedFrom":subQ3}),-1.0]])]});}
            extrude(context, id + "F33", {"entities" : qUnion([Q0]), "depth" : 25.4 * mm});
        }
        {
            var Q0;
            Q0=makeQuery(id+"F33.opExtrude","SWEPT_FACE",FACE,{"disambiguationData":[OSD([sQuery(id+"F32.wireOp",EDGE,"E52")])]});
            var sketch = newSketch(context, id + "F34", { "sketchPlane" : qUnion([Q0])});
            skCircle(sketch, "E61", {"center": v(-12.7, -215.46) * mm, "radius": 11.11 * mm});
            skPoint(sketch, "E61.centerSnap0", {"position": v(-12.7, -183.7) * mm});
            skPoint(sketch, "E62.startSnap0", {"position": v(-25.4, -272.6) * mm});
            skPoint(sketch, "E62.endSnap0", {"position": v(0, -272.6) * mm});
            skLineSegment(sketch, "E63", {"start": v(-12.7, -215.46) * mm, "end": v(-12.7, -323.4) * mm, "construction": true});
            skCircle(sketch, "E64", {"center": v(-12.7, -323.4) * mm, "radius": 11.11 * mm});
            skSolve(sketch);
        }
        {
            var Q0;
            Q0=makeQuery(id+"F34.imprint","IMPRINT",FACE,{"disambiguationData":[TD([[makeQuery(id+"F34.imprint","IMPRINT",EDGE,{"derivedFrom":sQuery(id+"F34.wireOp",EDGE,"E61")}),1.0]])]});
            var Q1;
            Q1=makeQuery(id+"F34.imprint","IMPRINT",FACE,{"disambiguationData":[TD([[makeQuery(id+"F34.imprint","IMPRINT",EDGE,{"derivedFrom":sQuery(id+"F34.wireOp",EDGE,"E64")}),1.0]])]});
            var Q2;
            Q2=makeQuery(id+"F33.opExtrude","SWEPT_FACE",FACE,{"disambiguationData":[OSD([sQuery(id+"F32.wireOp",EDGE,"E57.0")])]});
            extrude(context, id + "F35", {"entities" : qUnion([Q0, Q1]), "operationType" : NewBodyOperationType.REMOVE, "endBound" : BoundingType.UP_TO_SURFACE, "oppositeDirection" : true, "endBoundEntityFace" : qUnion([Q2]), "depth" : 25.4 * mm});
        }
        {
            var Q0;
            Q0=makeQuery(id+"F31.imprint","IMPRINT",FACE,{"disambiguationData":[TD([[makeQuery(id+"F31.imprint","IMPRINT",EDGE,{"derivedFrom":sQuery(id+"F31.wireOp",EDGE,"E49")}),1.0]])]});
            extrude(context, id + "F36", {"entities" : qUnion([Q0]), "depth" : 177.8 * mm});
        }
    });
